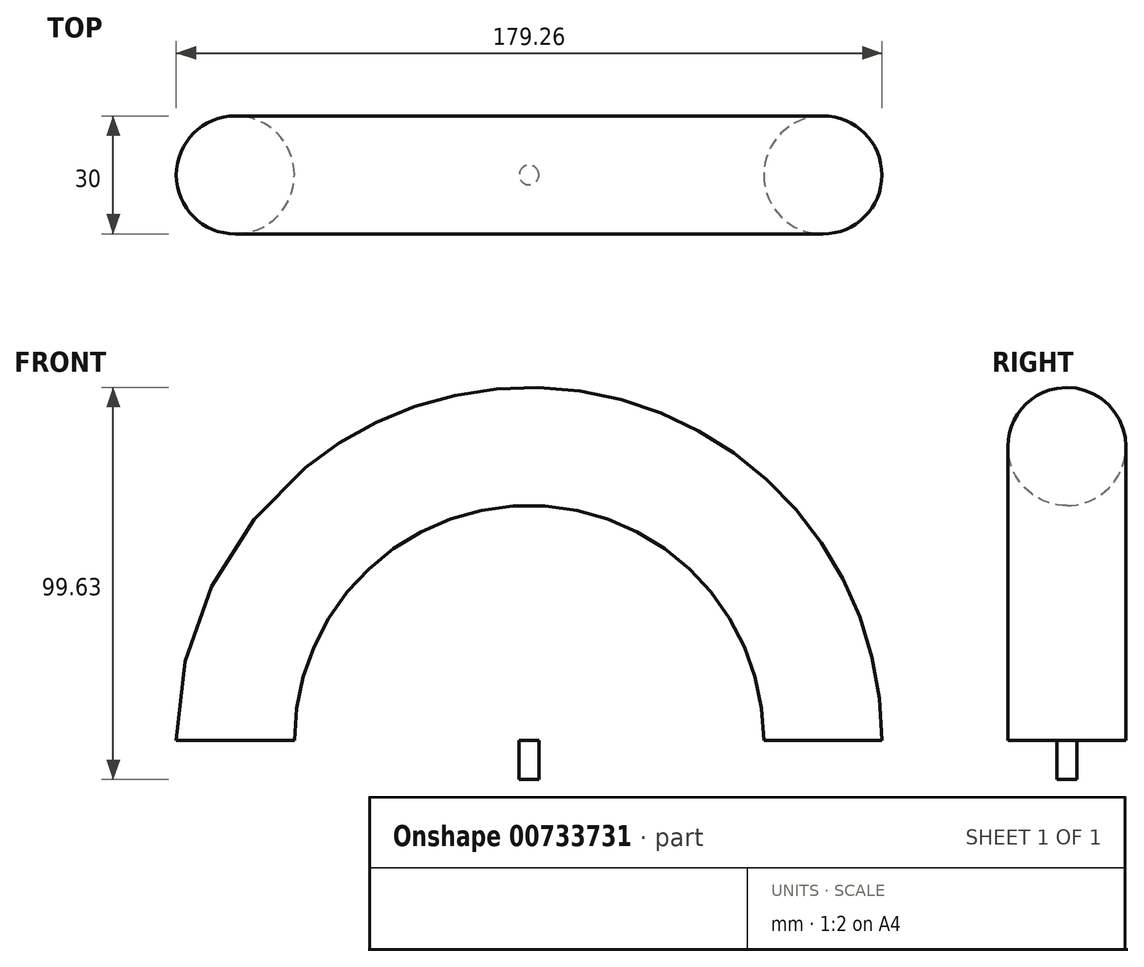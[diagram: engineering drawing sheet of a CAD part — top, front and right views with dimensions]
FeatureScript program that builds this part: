
annotation { "Feature Type Name" : "Feature", "Feature Type Description" : "" }
export const myFeature = defineFeature(function(context is Context, id is Id, definition is map)
    precondition{}
    {
        {
            var Q0;
            Q0=qCreatedBy(makeId("Front.planeOp"),FACE);
            var sketch = newSketch(context, id + "F0", { "sketchPlane" : qUnion([Q0])});
            skArc(sketch, "E0", {"start": v(75, 0) * mm, "mid": v(0, 75) * mm, "end": v(-75, 0) * mm});
            skLineSegment(sketch, "E1", {"start": v(0, 0) * mm, "end": v(75, 0) * mm});
            skLineSegment(sketch, "E2", {"start": v(0, 0) * mm, "end": v(-75, 0) * mm});
            skSolve(sketch);
        }
        {
            var Q0;
            Q0=qCreatedBy(makeId("Top.planeOp"),FACE);
            var sketch = newSketch(context, id + "F1", { "sketchPlane" : qUnion([Q0])});
            skCircle(sketch, "E3", {"center": v(-74.63, 0) * mm, "radius": 15 * mm});
            skCircle(sketch, "E4", {"center": v(0, 0) * mm, "radius": 2.5 * mm});
            skSolve(sketch);
        }
        {
            var Q0;
            Q0=makeQuery(id+"F1.imprint","IMPRINT",FACE,{"disambiguationData":[TD([[makeQuery(id+"F1.imprint","IMPRINT",EDGE,{"derivedFrom":sQuery(id+"F1.wireOp",EDGE,"E3")}),1.0]])]});
            var Q1;
            Q1=sQuery(id+"F0.wireOp",EDGE,"E0");
            sweep(context, id + "F2", {"profiles" : qUnion([Q0]), "path" : qUnion([Q1])});
        }
        {
            var Q0;
            Q0=makeQuery(id+"F1.imprint","IMPRINT",FACE,{"disambiguationData":[TD([[makeQuery(id+"F1.imprint","IMPRINT",EDGE,{"derivedFrom":sQuery(id+"F1.wireOp",EDGE,"E4")}),1.0]])]});
            extrude(context, id + "F3", {"entities" : qUnion([Q0]), "oppositeDirection" : true, "depth" : 10 * mm, "offsetDistance" : 25 * mm});
        }
    });
